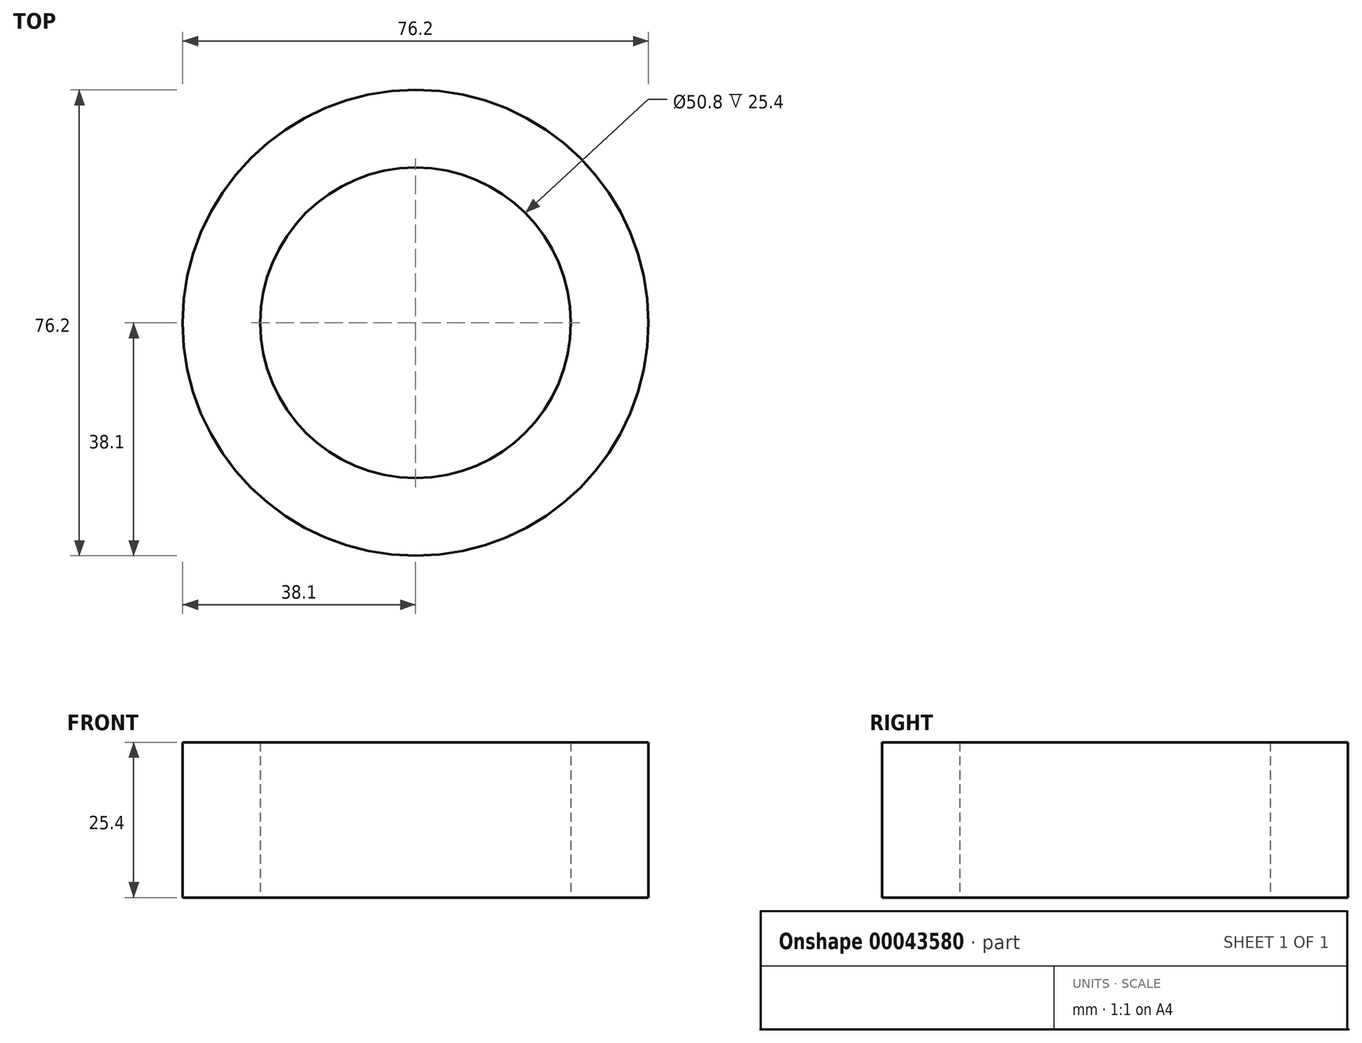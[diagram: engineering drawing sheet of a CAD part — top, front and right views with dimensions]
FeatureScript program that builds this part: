
annotation { "Feature Type Name" : "Feature", "Feature Type Description" : "" }
export const myFeature = defineFeature(function(context is Context, id is Id, definition is map)
    precondition{}
    {
        {
            var Q0;
            Q0=qCreatedBy(makeId("Top.planeOp"),FACE);
            var sketch = newSketch(context, id + "F0", { "sketchPlane" : qUnion([Q0])});
            skCircle(sketch, "E0", {"center": v(0, 0) * mm, "radius": 38.1 * mm});
            skCircle(sketch, "E1", {"center": v(0, 0) * mm, "radius": 25.4 * mm});
            skSolve(sketch);
        }
        {
            var Q0;
            Q0=makeQuery(id+"F0.imprint","IMPRINT",FACE,{"disambiguationData":[TD([[makeQuery(id+"F0.imprint","IMPRINT",EDGE,{"derivedFrom":sQuery(id+"F0.wireOp",EDGE,"E0")}),1.0]])]});
            extrude(context, id + "F1", {"entities" : qUnion([Q0]), "endBound" : BoundingType.SYMMETRIC, "depth" : 25.4 * mm, "hasSecondDirection" : true, "secondDirectionOppositeDirection" : true, "secondDirectionDepth" : 25.4 * mm});
        }
    });
